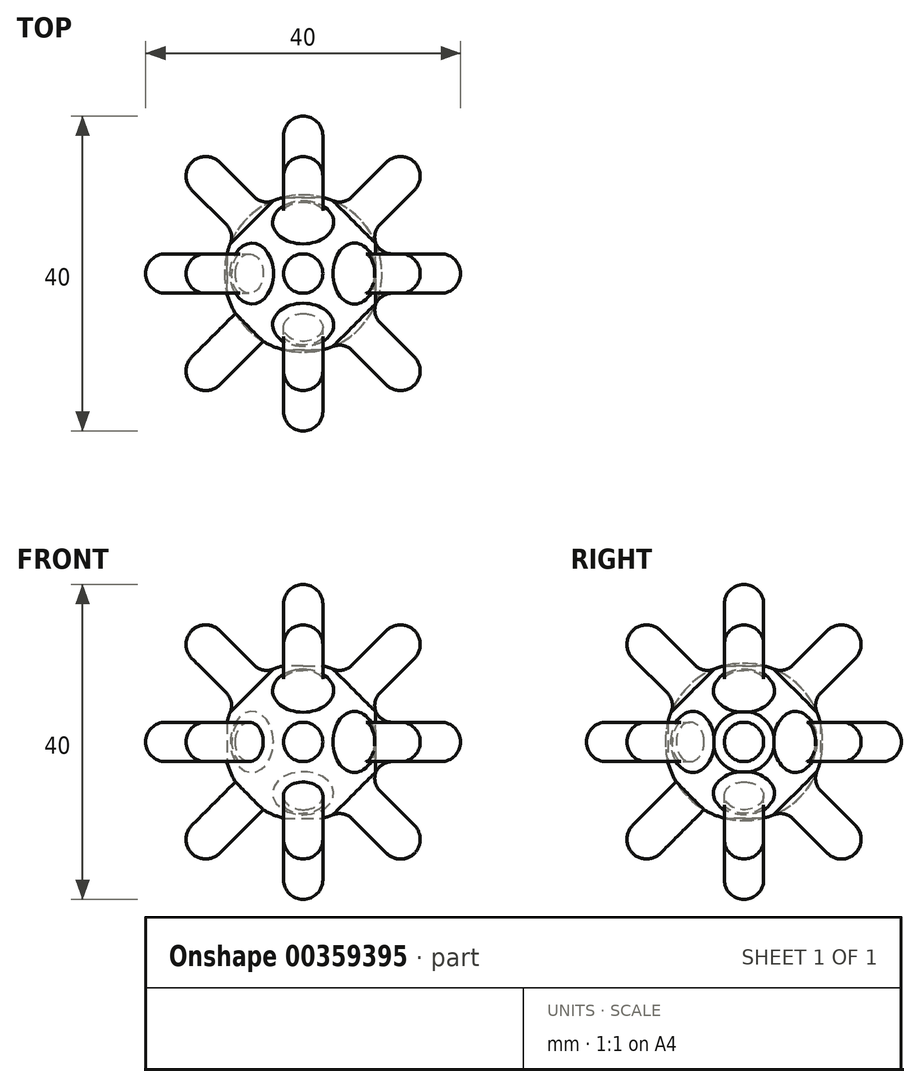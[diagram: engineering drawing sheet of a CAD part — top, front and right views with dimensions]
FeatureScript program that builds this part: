
annotation { "Feature Type Name" : "Feature", "Feature Type Description" : "" }
export const myFeature = defineFeature(function(context is Context, id is Id, definition is map)
    precondition{}
    {
        {
            var Q0;
            Q0=qCreatedBy(makeId("Front.planeOp"),FACE);
            var sketch = newSketch(context, id + "F0", { "sketchPlane" : qUnion([Q0])});
            skCircle(sketch, "E0", {"center": v(0, 0) * mm, "radius": 10 * mm});
            skSolve(sketch);
        }
        {
            var Q0;
            Q0=makeQuery(id+"F0.imprint","IMPRINT",FACE,{"disambiguationData":[TD([[makeQuery(id+"F0.imprint","IMPRINT",EDGE,{"derivedFrom":sQuery(id+"F0.wireOp",EDGE,"E0")}),1.0]])]});
            extrude(context, id + "F1", {"entities" : qUnion([Q0]), "endBound" : BoundingType.SYMMETRIC, "depth" : 20 * mm});
        }
        {
            var Q0;
            Q0=makeQuery(id+"F1.opExtrude","CAP_FACE",FACE,{"disambiguationData":[OSD([sQuery(id+"F0.wireOp",EDGE,"E0")])],"isStart":false});
            fillet(context, id + "F2", {"entities" : qUnion([Q0]), "radius" : 10 * mm, "tangentPropagation" : true, "allowEdgeOverflow" : false});
        }
        {
            var Q0;
            Q0=makeQuery(id+"F1.opExtrude","CAP_FACE",FACE,{"disambiguationData":[OSD([sQuery(id+"F0.wireOp",EDGE,"E0")])],"isStart":true});
            fillet(context, id + "F3", {"entities" : qUnion([Q0]), "radius" : 10 * mm, "tangentPropagation" : true, "allowEdgeOverflow" : false});
        }
        {
            var Q0;
            Q0=qCreatedBy(makeId("Front.planeOp"),FACE);
            var sketch = newSketch(context, id + "F4", { "sketchPlane" : qUnion([Q0])});
            skLineSegment(sketch, "E1", {"start": v(-14.14, 14.14) * mm, "end": v(-12.37, 15.9) * mm});
            skLineSegment(sketch, "E2", {"start": v(-14.14, 14.14) * mm, "end": v(-15.9, 12.37) * mm});
            skLineSegment(sketch, "E3", {"start": v(-20, 0) * mm, "end": v(-20, 2.5) * mm});
            skLineSegment(sketch, "E4", {"start": v(-20, 0) * mm, "end": v(-20, -2.5) * mm});
            skLineSegment(sketch, "E5", {"start": v(-14.14, -14.14) * mm, "end": v(-15.9, -12.37) * mm});
            skLineSegment(sketch, "E6", {"start": v(-14.14, -14.14) * mm, "end": v(-12.37, -15.9) * mm});
            skLineSegment(sketch, "E7", {"start": v(0, -20) * mm, "end": v(2.5, -20) * mm});
            skLineSegment(sketch, "E8", {"start": v(0, -20) * mm, "end": v(-2.5, -20) * mm});
            skLineSegment(sketch, "E9", {"start": v(14.14, -14.14) * mm, "end": v(12.37, -15.9) * mm});
            skLineSegment(sketch, "E10", {"start": v(14.14, -14.14) * mm, "end": v(15.9, -12.37) * mm});
            skLineSegment(sketch, "E11", {"start": v(20, 0) * mm, "end": v(20, -2.5) * mm});
            skLineSegment(sketch, "E12", {"start": v(20, 0) * mm, "end": v(20, 2.5) * mm});
            skLineSegment(sketch, "E13", {"start": v(0, 20) * mm, "end": v(2.5, 20) * mm});
            skLineSegment(sketch, "E14", {"start": v(0, 20) * mm, "end": v(-2.5, 20) * mm});
            skLineSegment(sketch, "E15", {"start": v(14.14, 14.14) * mm, "end": v(15.9, 12.37) * mm});
            skLineSegment(sketch, "E16", {"start": v(14.14, 14.14) * mm, "end": v(12.37, 15.9) * mm});
            skLineSegment(sketch, "E17", {"start": v(-15.9, 12.37) * mm, "end": v(-6.04, 2.5) * mm});
            skLineSegment(sketch, "E18", {"start": v(15.9, -12.37) * mm, "end": v(6.04, -2.5) * mm});
            skLineSegment(sketch, "E19", {"start": v(2.5, 20) * mm, "end": v(2.5, 6.04) * mm});
            skLineSegment(sketch, "E20", {"start": v(-2.5, 20) * mm, "end": v(-2.5, 6.04) * mm});
            skLineSegment(sketch, "E21", {"start": v(12.37, 15.9) * mm, "end": v(2.5, 6.04) * mm});
            skLineSegment(sketch, "E22", {"start": v(15.9, 12.37) * mm, "end": v(6.04, 2.5) * mm});
            skLineSegment(sketch, "E23", {"start": v(20, 2.5) * mm, "end": v(6.04, 2.5) * mm});
            skLineSegment(sketch, "E24", {"start": v(20, -2.5) * mm, "end": v(6.04, -2.5) * mm});
            skLineSegment(sketch, "E25.trimOffspring", {"start": v(-6.04, 2.5) * mm, "end": v(-20, 2.5) * mm});
            skLineSegment(sketch, "E26.trimOffspring", {"start": v(-2.5, 6.04) * mm, "end": v(-12.37, 15.9) * mm});
            skLineSegment(sketch, "E27.trimOffspring", {"start": v(-6.04, -2.5) * mm, "end": v(-15.9, -12.37) * mm});
            skLineSegment(sketch, "E28.trimOffspring", {"start": v(-6.04, -2.5) * mm, "end": v(-20, -2.5) * mm});
            skLineSegment(sketch, "E29.trimOffspring", {"start": v(-2.5, -6.04) * mm, "end": v(-2.5, -20) * mm});
            skLineSegment(sketch, "E30.trimOffspring", {"start": v(-2.5, -6.04) * mm, "end": v(-12.37, -15.9) * mm});
            skLineSegment(sketch, "E31.trimOffspring", {"start": v(2.5, -6.04) * mm, "end": v(12.37, -15.9) * mm});
            skLineSegment(sketch, "E32.trimOffspring", {"start": v(2.5, -6.04) * mm, "end": v(2.5, -20) * mm});
            skSolve(sketch);
        }
        {
            var Q0;
            Q0 = qSketchRegion(id + "F4", true);
            extrude(context, id + "F5", {"entities" : qUnion([Q0]), "operationType" : NewBodyOperationType.ADD, "endBound" : BoundingType.SYMMETRIC, "depth" : 5 * mm});
        }
        {
            var Q0;
            Q0=qCreatedBy(makeId("Top.planeOp"),FACE);
            var sketch = newSketch(context, id + "F6", { "sketchPlane" : qUnion([Q0])});
            skLineSegment(sketch, "E33", {"start": v(-14.14, 14.14) * mm, "end": v(-12.37, 15.9) * mm});
            skLineSegment(sketch, "E34", {"start": v(-14.14, 14.14) * mm, "end": v(-15.9, 12.37) * mm});
            skLineSegment(sketch, "E35", {"start": v(-20, 0) * mm, "end": v(-20, 2.5) * mm});
            skLineSegment(sketch, "E36", {"start": v(-20, 0) * mm, "end": v(-20, -2.5) * mm});
            skLineSegment(sketch, "E37", {"start": v(-14.14, -14.14) * mm, "end": v(-15.9, -12.37) * mm});
            skLineSegment(sketch, "E38", {"start": v(-14.14, -14.14) * mm, "end": v(-12.37, -15.9) * mm});
            skLineSegment(sketch, "E39", {"start": v(0, -20) * mm, "end": v(2.5, -20) * mm});
            skLineSegment(sketch, "E40", {"start": v(0, -20) * mm, "end": v(-2.5, -20) * mm});
            skLineSegment(sketch, "E41", {"start": v(14.14, -14.14) * mm, "end": v(12.37, -15.9) * mm});
            skLineSegment(sketch, "E42", {"start": v(14.14, -14.14) * mm, "end": v(15.9, -12.37) * mm});
            skLineSegment(sketch, "E43", {"start": v(20, 0) * mm, "end": v(20, -2.5) * mm});
            skLineSegment(sketch, "E44", {"start": v(20, 0) * mm, "end": v(20, 2.5) * mm});
            skLineSegment(sketch, "E45", {"start": v(0, 20) * mm, "end": v(2.5, 20) * mm});
            skLineSegment(sketch, "E46", {"start": v(0, 20) * mm, "end": v(-2.5, 20) * mm});
            skLineSegment(sketch, "E47", {"start": v(14.14, 14.14) * mm, "end": v(15.9, 12.37) * mm});
            skLineSegment(sketch, "E48", {"start": v(14.14, 14.14) * mm, "end": v(12.37, 15.9) * mm});
            skLineSegment(sketch, "E49", {"start": v(-15.9, 12.37) * mm, "end": v(-6.04, 2.5) * mm});
            skLineSegment(sketch, "E50", {"start": v(15.9, -12.37) * mm, "end": v(6.04, -2.5) * mm});
            skLineSegment(sketch, "E51", {"start": v(2.5, 20) * mm, "end": v(2.5, 6.04) * mm});
            skLineSegment(sketch, "E52", {"start": v(-2.5, 20) * mm, "end": v(-2.5, 6.04) * mm});
            skLineSegment(sketch, "E53", {"start": v(12.37, 15.9) * mm, "end": v(2.5, 6.04) * mm});
            skLineSegment(sketch, "E54", {"start": v(15.9, 12.37) * mm, "end": v(6.04, 2.5) * mm});
            skLineSegment(sketch, "E55", {"start": v(20, 2.5) * mm, "end": v(6.04, 2.5) * mm});
            skLineSegment(sketch, "E56", {"start": v(20, -2.5) * mm, "end": v(6.04, -2.5) * mm});
            skLineSegment(sketch, "E57.trimOffspring", {"start": v(-6.04, 2.5) * mm, "end": v(-20, 2.5) * mm});
            skLineSegment(sketch, "E58.trimOffspring", {"start": v(-2.5, 6.04) * mm, "end": v(-12.37, 15.9) * mm});
            skLineSegment(sketch, "E59.trimOffspring", {"start": v(-6.04, -2.5) * mm, "end": v(-15.9, -12.37) * mm});
            skLineSegment(sketch, "E60.trimOffspring", {"start": v(-6.04, -2.5) * mm, "end": v(-20, -2.5) * mm});
            skLineSegment(sketch, "E61.trimOffspring", {"start": v(-2.5, -6.04) * mm, "end": v(-2.5, -20) * mm});
            skLineSegment(sketch, "E62.trimOffspring", {"start": v(-2.5, -6.04) * mm, "end": v(-12.37, -15.9) * mm});
            skLineSegment(sketch, "E63.trimOffspring", {"start": v(2.5, -6.04) * mm, "end": v(12.37, -15.9) * mm});
            skLineSegment(sketch, "E64.trimOffspring", {"start": v(2.5, -6.04) * mm, "end": v(2.5, -20) * mm});
            skSolve(sketch);
        }
        {
            var Q0;
            Q0=makeQuery(id+"F6.imprint","IMPRINT",FACE,{"disambiguationData":[TD([[makeQuery(id+"F6.imprint","IMPRINT",EDGE,{"derivedFrom":sQuery(id+"F6.wireOp",EDGE,"E33")}),-1.0]])]});
            extrude(context, id + "F7", {"entities" : qUnion([Q0]), "operationType" : NewBodyOperationType.ADD, "endBound" : BoundingType.SYMMETRIC, "depth" : 5 * mm});
        }
        {
            var Q0;
            Q0=qCreatedBy(makeId("Right.planeOp"),FACE);
            var sketch = newSketch(context, id + "F8", { "sketchPlane" : qUnion([Q0])});
            skLineSegment(sketch, "E65", {"start": v(-14.14, 14.14) * mm, "end": v(-12.37, 15.9) * mm});
            skLineSegment(sketch, "E66", {"start": v(-14.14, 14.14) * mm, "end": v(-15.9, 12.37) * mm});
            skLineSegment(sketch, "E67", {"start": v(-20, 0) * mm, "end": v(-20, 2.5) * mm});
            skLineSegment(sketch, "E68", {"start": v(-20, 0) * mm, "end": v(-20, -2.5) * mm});
            skLineSegment(sketch, "E69", {"start": v(-14.14, -14.14) * mm, "end": v(-15.9, -12.37) * mm});
            skLineSegment(sketch, "E70", {"start": v(-14.14, -14.14) * mm, "end": v(-12.37, -15.9) * mm});
            skLineSegment(sketch, "E71", {"start": v(0, -20) * mm, "end": v(2.5, -20) * mm});
            skLineSegment(sketch, "E72", {"start": v(0, -20) * mm, "end": v(-2.5, -20) * mm});
            skLineSegment(sketch, "E73", {"start": v(14.14, -14.14) * mm, "end": v(12.37, -15.9) * mm});
            skLineSegment(sketch, "E74", {"start": v(14.14, -14.14) * mm, "end": v(15.9, -12.37) * mm});
            skLineSegment(sketch, "E75", {"start": v(20, 0) * mm, "end": v(20, -2.5) * mm});
            skLineSegment(sketch, "E76", {"start": v(20, 0) * mm, "end": v(20, 2.5) * mm});
            skLineSegment(sketch, "E77", {"start": v(0, 20) * mm, "end": v(2.5, 20) * mm});
            skLineSegment(sketch, "E78", {"start": v(0, 20) * mm, "end": v(-2.5, 20) * mm});
            skLineSegment(sketch, "E79", {"start": v(14.14, 14.14) * mm, "end": v(15.9, 12.37) * mm});
            skLineSegment(sketch, "E80", {"start": v(14.14, 14.14) * mm, "end": v(12.37, 15.9) * mm});
            skLineSegment(sketch, "E81", {"start": v(-15.9, 12.37) * mm, "end": v(-6.04, 2.5) * mm});
            skLineSegment(sketch, "E82", {"start": v(15.9, -12.37) * mm, "end": v(6.04, -2.5) * mm});
            skLineSegment(sketch, "E83", {"start": v(2.5, 20) * mm, "end": v(2.5, 6.04) * mm});
            skLineSegment(sketch, "E84", {"start": v(-2.5, 20) * mm, "end": v(-2.5, 6.04) * mm});
            skLineSegment(sketch, "E85", {"start": v(12.37, 15.9) * mm, "end": v(2.5, 6.04) * mm});
            skLineSegment(sketch, "E86", {"start": v(15.9, 12.37) * mm, "end": v(6.04, 2.5) * mm});
            skLineSegment(sketch, "E87", {"start": v(20, 2.5) * mm, "end": v(6.04, 2.5) * mm});
            skLineSegment(sketch, "E88", {"start": v(20, -2.5) * mm, "end": v(6.04, -2.5) * mm});
            skLineSegment(sketch, "E89.trimOffspring", {"start": v(-6.04, 2.5) * mm, "end": v(-20, 2.5) * mm});
            skLineSegment(sketch, "E90.trimOffspring", {"start": v(-2.5, 6.04) * mm, "end": v(-12.37, 15.9) * mm});
            skLineSegment(sketch, "E91.trimOffspring", {"start": v(-6.04, -2.5) * mm, "end": v(-15.9, -12.37) * mm});
            skLineSegment(sketch, "E92.trimOffspring", {"start": v(-6.04, -2.5) * mm, "end": v(-20, -2.5) * mm});
            skLineSegment(sketch, "E93.trimOffspring", {"start": v(-2.5, -6.04) * mm, "end": v(-2.5, -20) * mm});
            skLineSegment(sketch, "E94.trimOffspring", {"start": v(-2.5, -6.04) * mm, "end": v(-12.37, -15.9) * mm});
            skLineSegment(sketch, "E95.trimOffspring", {"start": v(2.5, -6.04) * mm, "end": v(12.37, -15.9) * mm});
            skLineSegment(sketch, "E96.trimOffspring", {"start": v(2.5, -6.04) * mm, "end": v(2.5, -20) * mm});
            skSolve(sketch);
        }
        {
            var Q0;
            Q0 = qSketchRegion(id + "F8", true);
            extrude(context, id + "F9", {"entities" : qUnion([Q0]), "operationType" : NewBodyOperationType.ADD, "endBound" : BoundingType.SYMMETRIC, "depth" : 5 * mm});
        }
        {
            var Q0;
            Q0=makeQuery(id+"F5.opExtrude","CAP_EDGE",EDGE,{"disambiguationData":[OSD([sQuery(id+"F4.wireOp",EDGE,"E23")])],"isStart":false});
            var Q1;
            Q1=makeQuery(id+"F5.opExtrude","CAP_EDGE",EDGE,{"disambiguationData":[OSD([sQuery(id+"F4.wireOp",EDGE,"E24")])],"isStart":false});
            var Q2;
            Q2=makeQuery(id+"F5.opExtrude","CAP_EDGE",EDGE,{"disambiguationData":[OSD([sQuery(id+"F4.wireOp",EDGE,"E23")])],"isStart":true});
            var Q3;
            Q3=makeQuery(id+"F5.opExtrude","CAP_EDGE",EDGE,{"disambiguationData":[OSD([sQuery(id+"F4.wireOp",EDGE,"E24")])],"isStart":true});
            var Q4;
            Q4=makeQuery(id+"F5.opExtrude","SWEPT_FACE",FACE,{"disambiguationData":[OSD([sQuery(id+"F4.wireOp",EDGE,"E11"),sQuery(id+"F4.wireOp",EDGE,"E12")])]});
            fillet(context, id + "F10", {"entities" : qUnion([Q0, Q1, Q2, Q3, Q4]), "radius" : 2.5 * mm, "tangentPropagation" : true, "allowEdgeOverflow" : false});
        }
        {
            var Q0;
            Q0=makeQuery(id+"F5.opExtrude","SWEPT_FACE",FACE,{"disambiguationData":[OSD([sQuery(id+"F4.wireOp",EDGE,"E9"),sQuery(id+"F4.wireOp",EDGE,"E10")])]});
            var Q1;
            Q1=makeQuery(id+"F5.opExtrude","CAP_EDGE",EDGE,{"disambiguationData":[OSD([sQuery(id+"F4.wireOp",EDGE,"E31.trimOffspring")])],"isStart":false});
            var Q2;
            Q2=makeQuery(id+"F5.opExtrude","CAP_EDGE",EDGE,{"disambiguationData":[OSD([sQuery(id+"F4.wireOp",EDGE,"E31.trimOffspring")])],"isStart":true});
            var Q3;
            Q3=makeQuery(id+"F5.opExtrude","CAP_EDGE",EDGE,{"disambiguationData":[OSD([sQuery(id+"F4.wireOp",EDGE,"E18")])],"isStart":false});
            var Q4;
            Q4=makeQuery(id+"F5.opExtrude","CAP_EDGE",EDGE,{"disambiguationData":[OSD([sQuery(id+"F4.wireOp",EDGE,"E18")])],"isStart":true});
            fillet(context, id + "F11", {"entities" : qUnion([Q0, Q1, Q2, Q3, Q4]), "radius" : 2.5 * mm, "tangentPropagation" : true, "allowEdgeOverflow" : false});
        }
        {
            var Q0;
            Q0=makeQuery(id+"F5.opExtrude","CAP_EDGE",EDGE,{"disambiguationData":[OSD([sQuery(id+"F4.wireOp",EDGE,"E22")])],"isStart":false});
            var Q1;
            Q1=makeQuery(id+"F5.opExtrude","CAP_EDGE",EDGE,{"disambiguationData":[OSD([sQuery(id+"F4.wireOp",EDGE,"E22")])],"isStart":true});
            var Q2;
            Q2=makeQuery(id+"F5.opExtrude","CAP_EDGE",EDGE,{"disambiguationData":[OSD([sQuery(id+"F4.wireOp",EDGE,"E21")])],"isStart":false});
            var Q3;
            Q3=makeQuery(id+"F5.opExtrude","CAP_EDGE",EDGE,{"disambiguationData":[OSD([sQuery(id+"F4.wireOp",EDGE,"E21")])],"isStart":true});
            var Q4;
            Q4=makeQuery(id+"F5.opExtrude","SWEPT_FACE",FACE,{"disambiguationData":[OSD([sQuery(id+"F4.wireOp",EDGE,"E15"),sQuery(id+"F4.wireOp",EDGE,"E16")])]});
            fillet(context, id + "F12", {"entities" : qUnion([Q0, Q1, Q2, Q3, Q4]), "radius" : 2.5 * mm, "tangentPropagation" : true, "allowEdgeOverflow" : false});
        }
        {
            var Q0;
            Q0=makeQuery(id+"F5.opExtrude","CAP_EDGE",EDGE,{"disambiguationData":[OSD([sQuery(id+"F4.wireOp",EDGE,"E19")])],"isStart":false});
            var Q1;
            Q1=makeQuery(id+"F5.opExtrude","CAP_EDGE",EDGE,{"disambiguationData":[OSD([sQuery(id+"F4.wireOp",EDGE,"E20")])],"isStart":false});
            var Q2;
            Q2=makeQuery(id+"F5.opExtrude","CAP_EDGE",EDGE,{"disambiguationData":[OSD([sQuery(id+"F4.wireOp",EDGE,"E19")])],"isStart":true});
            var Q3;
            Q3=makeQuery(id+"F5.opExtrude","CAP_EDGE",EDGE,{"disambiguationData":[OSD([sQuery(id+"F4.wireOp",EDGE,"E20")])],"isStart":true});
            var Q4;
            Q4=makeQuery(id+"F5.opExtrude","SWEPT_FACE",FACE,{"disambiguationData":[OSD([sQuery(id+"F4.wireOp",EDGE,"E13"),sQuery(id+"F4.wireOp",EDGE,"E14")])]});
            fillet(context, id + "F13", {"entities" : qUnion([Q0, Q1, Q2, Q3, Q4]), "radius" : 2.5 * mm, "tangentPropagation" : true, "allowEdgeOverflow" : false});
        }
        {
            var Q0;
            Q0=makeQuery(id+"F5.opExtrude","CAP_EDGE",EDGE,{"disambiguationData":[OSD([sQuery(id+"F4.wireOp",EDGE,"E32.trimOffspring")])],"isStart":false});
            var Q1;
            Q1=makeQuery(id+"F5.opExtrude","CAP_EDGE",EDGE,{"disambiguationData":[OSD([sQuery(id+"F4.wireOp",EDGE,"E32.trimOffspring")])],"isStart":true});
            var Q2;
            Q2=makeQuery(id+"F5.opExtrude","CAP_EDGE",EDGE,{"disambiguationData":[OSD([sQuery(id+"F4.wireOp",EDGE,"E29.trimOffspring")])],"isStart":false});
            var Q3;
            Q3=makeQuery(id+"F5.opExtrude","CAP_EDGE",EDGE,{"disambiguationData":[OSD([sQuery(id+"F4.wireOp",EDGE,"E29.trimOffspring")])],"isStart":true});
            var Q4;
            Q4=makeQuery(id+"F5.opExtrude","SWEPT_FACE",FACE,{"disambiguationData":[OSD([sQuery(id+"F4.wireOp",EDGE,"E7"),sQuery(id+"F4.wireOp",EDGE,"E8")])]});
            fillet(context, id + "F14", {"entities" : qUnion([Q0, Q1, Q2, Q3, Q4]), "radius" : 2.5 * mm, "tangentPropagation" : true, "allowEdgeOverflow" : false});
        }
        {
            var Q0;
            Q0=makeQuery(id+"F5.opExtrude","CAP_EDGE",EDGE,{"disambiguationData":[OSD([sQuery(id+"F4.wireOp",EDGE,"E27.trimOffspring")])],"isStart":true});
            var Q1;
            Q1=makeQuery(id+"F5.opExtrude","CAP_EDGE",EDGE,{"disambiguationData":[OSD([sQuery(id+"F4.wireOp",EDGE,"E27.trimOffspring")])],"isStart":false});
            var Q2;
            Q2=makeQuery(id+"F5.opExtrude","CAP_EDGE",EDGE,{"disambiguationData":[OSD([sQuery(id+"F4.wireOp",EDGE,"E30.trimOffspring")])],"isStart":true});
            var Q3;
            Q3=makeQuery(id+"F5.opExtrude","CAP_EDGE",EDGE,{"disambiguationData":[OSD([sQuery(id+"F4.wireOp",EDGE,"E30.trimOffspring")])],"isStart":false});
            var Q4;
            Q4=makeQuery(id+"F5.opExtrude","SWEPT_FACE",FACE,{"disambiguationData":[OSD([sQuery(id+"F4.wireOp",EDGE,"E5"),sQuery(id+"F4.wireOp",EDGE,"E6")])]});
            fillet(context, id + "F15", {"entities" : qUnion([Q0, Q1, Q2, Q3, Q4]), "radius" : 2.5 * mm, "tangentPropagation" : true, "allowEdgeOverflow" : false});
        }
        {
            var Q0;
            Q0=makeQuery(id+"F5.opExtrude","CAP_EDGE",EDGE,{"disambiguationData":[OSD([sQuery(id+"F4.wireOp",EDGE,"E28.trimOffspring")])],"isStart":false});
            var Q1;
            Q1=makeQuery(id+"F5.opExtrude","CAP_EDGE",EDGE,{"disambiguationData":[OSD([sQuery(id+"F4.wireOp",EDGE,"E28.trimOffspring")])],"isStart":true});
            var Q2;
            Q2=makeQuery(id+"F5.opExtrude","CAP_EDGE",EDGE,{"disambiguationData":[OSD([sQuery(id+"F4.wireOp",EDGE,"E25.trimOffspring")])],"isStart":false});
            var Q3;
            Q3=makeQuery(id+"F5.opExtrude","CAP_EDGE",EDGE,{"disambiguationData":[OSD([sQuery(id+"F4.wireOp",EDGE,"E25.trimOffspring")])],"isStart":true});
            var Q4;
            Q4=makeQuery(id+"F5.opExtrude","SWEPT_FACE",FACE,{"disambiguationData":[OSD([sQuery(id+"F4.wireOp",EDGE,"E3"),sQuery(id+"F4.wireOp",EDGE,"E4")])]});
            fillet(context, id + "F16", {"entities" : qUnion([Q0, Q1, Q2, Q3, Q4]), "radius" : 2.5 * mm, "tangentPropagation" : true, "allowEdgeOverflow" : false});
        }
        {
            var Q0;
            Q0=makeQuery(id+"F5.opExtrude","CAP_EDGE",EDGE,{"disambiguationData":[OSD([sQuery(id+"F4.wireOp",EDGE,"E26.trimOffspring")])],"isStart":false});
            var Q1;
            Q1=makeQuery(id+"F5.opExtrude","CAP_EDGE",EDGE,{"disambiguationData":[OSD([sQuery(id+"F4.wireOp",EDGE,"E26.trimOffspring")])],"isStart":true});
            var Q2;
            Q2=makeQuery(id+"F5.opExtrude","CAP_EDGE",EDGE,{"disambiguationData":[OSD([sQuery(id+"F4.wireOp",EDGE,"E17")])],"isStart":false});
            var Q3;
            Q3=makeQuery(id+"F5.opExtrude","SWEPT_FACE",FACE,{"disambiguationData":[OSD([sQuery(id+"F4.wireOp",EDGE,"E1"),sQuery(id+"F4.wireOp",EDGE,"E2")])]});
            var Q4;
            Q4=makeQuery(id+"F5.opExtrude","CAP_EDGE",EDGE,{"disambiguationData":[OSD([sQuery(id+"F4.wireOp",EDGE,"E17")])],"isStart":true});
            fillet(context, id + "F17", {"entities" : qUnion([Q0, Q1, Q2, Q3, Q4]), "radius" : 2.5 * mm, "tangentPropagation" : true, "allowEdgeOverflow" : false});
        }
        {
            var Q0;
            Q0=makeQuery(id+"F9.opExtrude","CAP_EDGE",EDGE,{"disambiguationData":[OSD([sQuery(id+"F8.wireOp",EDGE,"E95.trimOffspring")])],"isStart":false});
            var Q1;
            Q1=makeQuery(id+"F9.opExtrude","CAP_EDGE",EDGE,{"disambiguationData":[OSD([sQuery(id+"F8.wireOp",EDGE,"E82")])],"isStart":false});
            var Q2;
            Q2=makeQuery(id+"F9.opExtrude","SWEPT_FACE",FACE,{"disambiguationData":[OSD([sQuery(id+"F8.wireOp",EDGE,"E73"),sQuery(id+"F8.wireOp",EDGE,"E74")])]});
            var Q3;
            Q3=makeQuery(id+"F9.opExtrude","CAP_EDGE",EDGE,{"disambiguationData":[OSD([sQuery(id+"F8.wireOp",EDGE,"E82")])],"isStart":true});
            var Q4;
            Q4=makeQuery(id+"F9.opExtrude","CAP_EDGE",EDGE,{"disambiguationData":[OSD([sQuery(id+"F8.wireOp",EDGE,"E95.trimOffspring")])],"isStart":true});
            fillet(context, id + "F18", {"entities" : qUnion([Q0, Q1, Q2, Q3, Q4]), "radius" : 2.5 * mm, "tangentPropagation" : true, "allowEdgeOverflow" : false});
        }
        {
            var Q0;
            Q0=makeQuery(id+"F7.opExtrude","CAP_EDGE",EDGE,{"disambiguationData":[OSD([sQuery(id+"F6.wireOp",EDGE,"E52")])],"isStart":false});
            var Q1;
            Q1=makeQuery(id+"F7.opExtrude","CAP_EDGE",EDGE,{"disambiguationData":[OSD([sQuery(id+"F6.wireOp",EDGE,"E52")])],"isStart":true});
            var Q2;
            Q2=makeQuery(id+"F7.opExtrude","CAP_EDGE",EDGE,{"disambiguationData":[OSD([sQuery(id+"F6.wireOp",EDGE,"E51")])],"isStart":false});
            var Q3;
            Q3=makeQuery(id+"F7.opExtrude","CAP_EDGE",EDGE,{"disambiguationData":[OSD([sQuery(id+"F6.wireOp",EDGE,"E51")])],"isStart":true});
            var Q4;
            Q4=makeQuery(id+"F7.opExtrude","SWEPT_FACE",FACE,{"disambiguationData":[OSD([sQuery(id+"F6.wireOp",EDGE,"E45"),sQuery(id+"F6.wireOp",EDGE,"E46")])]});
            fillet(context, id + "F19", {"entities" : qUnion([Q0, Q1, Q2, Q3, Q4]), "radius" : 2.5 * mm, "tangentPropagation" : true, "allowEdgeOverflow" : false});
        }
        {
            var Q0;
            Q0=makeQuery(id+"F9.opExtrude","CAP_EDGE",EDGE,{"disambiguationData":[OSD([sQuery(id+"F8.wireOp",EDGE,"E85")])],"isStart":true});
            var Q1;
            Q1=makeQuery(id+"F9.opExtrude","CAP_EDGE",EDGE,{"disambiguationData":[OSD([sQuery(id+"F8.wireOp",EDGE,"E85")])],"isStart":false});
            var Q2;
            Q2=makeQuery(id+"F9.opExtrude","CAP_EDGE",EDGE,{"disambiguationData":[OSD([sQuery(id+"F8.wireOp",EDGE,"E86")])],"isStart":true});
            var Q3;
            Q3=makeQuery(id+"F9.opExtrude","CAP_EDGE",EDGE,{"disambiguationData":[OSD([sQuery(id+"F8.wireOp",EDGE,"E86")])],"isStart":false});
            var Q4;
            Q4=makeQuery(id+"F9.opExtrude","SWEPT_FACE",FACE,{"disambiguationData":[OSD([sQuery(id+"F8.wireOp",EDGE,"E79"),sQuery(id+"F8.wireOp",EDGE,"E80")])]});
            fillet(context, id + "F20", {"entities" : qUnion([Q0, Q1, Q2, Q3, Q4]), "radius" : 2.5 * mm, "tangentPropagation" : true, "allowEdgeOverflow" : false});
        }
        {
            var Q0;
            Q0=makeQuery(id+"F9.opExtrude","CAP_EDGE",EDGE,{"disambiguationData":[OSD([sQuery(id+"F8.wireOp",EDGE,"E81")])],"isStart":true});
            var Q1;
            Q1=makeQuery(id+"F9.opExtrude","CAP_EDGE",EDGE,{"disambiguationData":[OSD([sQuery(id+"F8.wireOp",EDGE,"E81")])],"isStart":false});
            var Q2;
            Q2=makeQuery(id+"F9.opExtrude","CAP_EDGE",EDGE,{"disambiguationData":[OSD([sQuery(id+"F8.wireOp",EDGE,"E90.trimOffspring")])],"isStart":false});
            var Q3;
            Q3=makeQuery(id+"F9.opExtrude","CAP_EDGE",EDGE,{"disambiguationData":[OSD([sQuery(id+"F8.wireOp",EDGE,"E90.trimOffspring")])],"isStart":true});
            var Q4;
            Q4=makeQuery(id+"F9.opExtrude","SWEPT_FACE",FACE,{"disambiguationData":[OSD([sQuery(id+"F8.wireOp",EDGE,"E65"),sQuery(id+"F8.wireOp",EDGE,"E66")])]});
            fillet(context, id + "F21", {"entities" : qUnion([Q0, Q1, Q2, Q3, Q4]), "radius" : 2.5 * mm, "tangentPropagation" : true, "allowEdgeOverflow" : false});
        }
        {
            var Q0;
            Q0=makeQuery(id+"F7.opExtrude","CAP_EDGE",EDGE,{"disambiguationData":[OSD([sQuery(id+"F6.wireOp",EDGE,"E64.trimOffspring")])],"isStart":false});
            var Q1;
            Q1=makeQuery(id+"F7.opExtrude","CAP_EDGE",EDGE,{"disambiguationData":[OSD([sQuery(id+"F6.wireOp",EDGE,"E61.trimOffspring")])],"isStart":false});
            var Q2;
            Q2=makeQuery(id+"F7.opExtrude","CAP_EDGE",EDGE,{"disambiguationData":[OSD([sQuery(id+"F6.wireOp",EDGE,"E61.trimOffspring")])],"isStart":true});
            var Q3;
            Q3=makeQuery(id+"F7.opExtrude","CAP_EDGE",EDGE,{"disambiguationData":[OSD([sQuery(id+"F6.wireOp",EDGE,"E64.trimOffspring")])],"isStart":true});
            var Q4;
            Q4=makeQuery(id+"F7.opExtrude","SWEPT_FACE",FACE,{"disambiguationData":[OSD([sQuery(id+"F6.wireOp",EDGE,"E39"),sQuery(id+"F6.wireOp",EDGE,"E40")])]});
            fillet(context, id + "F22", {"entities" : qUnion([Q0, Q1, Q2, Q3, Q4]), "radius" : 2.5 * mm, "tangentPropagation" : true, "allowEdgeOverflow" : false});
        }
        {
            var Q0;
            Q0=makeQuery(id+"F9.opExtrude","CAP_EDGE",EDGE,{"disambiguationData":[OSD([sQuery(id+"F8.wireOp",EDGE,"E91.trimOffspring")])],"isStart":true});
            var Q1;
            Q1=makeQuery(id+"F9.opExtrude","CAP_EDGE",EDGE,{"disambiguationData":[OSD([sQuery(id+"F8.wireOp",EDGE,"E91.trimOffspring")])],"isStart":false});
            var Q2;
            Q2=makeQuery(id+"F9.opExtrude","CAP_EDGE",EDGE,{"disambiguationData":[OSD([sQuery(id+"F8.wireOp",EDGE,"E94.trimOffspring")])],"isStart":true});
            var Q3;
            Q3=makeQuery(id+"F9.opExtrude","CAP_EDGE",EDGE,{"disambiguationData":[OSD([sQuery(id+"F8.wireOp",EDGE,"E94.trimOffspring")])],"isStart":false});
            var Q4;
            Q4=makeQuery(id+"F9.opExtrude","SWEPT_FACE",FACE,{"disambiguationData":[OSD([sQuery(id+"F8.wireOp",EDGE,"E69"),sQuery(id+"F8.wireOp",EDGE,"E70")])]});
            fillet(context, id + "F23", {"entities" : qUnion([Q0, Q1, Q2, Q3, Q4]), "radius" : 2.5 * mm, "tangentPropagation" : true, "allowEdgeOverflow" : false});
        }
        {
            var Q0;
            Q0=makeQuery(id+"F7.opExtrude","CAP_EDGE",EDGE,{"disambiguationData":[OSD([sQuery(id+"F6.wireOp",EDGE,"E62.trimOffspring")])],"isStart":true});
            var Q1;
            Q1=makeQuery(id+"F7.opExtrude","CAP_EDGE",EDGE,{"disambiguationData":[OSD([sQuery(id+"F6.wireOp",EDGE,"E62.trimOffspring")])],"isStart":false});
            var Q2;
            Q2=makeQuery(id+"F7.opExtrude","CAP_EDGE",EDGE,{"disambiguationData":[OSD([sQuery(id+"F6.wireOp",EDGE,"E59.trimOffspring")])],"isStart":true});
            var Q3;
            Q3=makeQuery(id+"F7.opExtrude","CAP_EDGE",EDGE,{"disambiguationData":[OSD([sQuery(id+"F6.wireOp",EDGE,"E59.trimOffspring")])],"isStart":false});
            var Q4;
            Q4=makeQuery(id+"F7.opExtrude","SWEPT_FACE",FACE,{"disambiguationData":[OSD([sQuery(id+"F6.wireOp",EDGE,"E37"),sQuery(id+"F6.wireOp",EDGE,"E38")])]});
            fillet(context, id + "F24", {"entities" : qUnion([Q0, Q1, Q2, Q3, Q4]), "radius" : 2.5 * mm, "tangentPropagation" : true, "allowEdgeOverflow" : false});
        }
        {
            var Q0;
            Q0=makeQuery(id+"F7.opExtrude","CAP_EDGE",EDGE,{"disambiguationData":[OSD([sQuery(id+"F6.wireOp",EDGE,"E49")])],"isStart":true});
            var Q1;
            Q1=makeQuery(id+"F7.opExtrude","CAP_EDGE",EDGE,{"disambiguationData":[OSD([sQuery(id+"F6.wireOp",EDGE,"E49")])],"isStart":false});
            var Q2;
            Q2=makeQuery(id+"F7.opExtrude","CAP_EDGE",EDGE,{"disambiguationData":[OSD([sQuery(id+"F6.wireOp",EDGE,"E58.trimOffspring")])],"isStart":true});
            var Q3;
            Q3=makeQuery(id+"F7.opExtrude","CAP_EDGE",EDGE,{"disambiguationData":[OSD([sQuery(id+"F6.wireOp",EDGE,"E58.trimOffspring")])],"isStart":false});
            var Q4;
            Q4=makeQuery(id+"F7.opExtrude","SWEPT_FACE",FACE,{"disambiguationData":[OSD([sQuery(id+"F6.wireOp",EDGE,"E33"),sQuery(id+"F6.wireOp",EDGE,"E34")])]});
            fillet(context, id + "F25", {"entities" : qUnion([Q0, Q1, Q2, Q3, Q4]), "radius" : 2.5 * mm, "tangentPropagation" : true, "allowEdgeOverflow" : false});
        }
        {
            var Q0;
            Q0=makeQuery(id+"F7.opExtrude","CAP_EDGE",EDGE,{"disambiguationData":[OSD([sQuery(id+"F6.wireOp",EDGE,"E53")])],"isStart":true});
            var Q1;
            Q1=makeQuery(id+"F7.opExtrude","CAP_EDGE",EDGE,{"disambiguationData":[OSD([sQuery(id+"F6.wireOp",EDGE,"E53")])],"isStart":false});
            var Q2;
            Q2=makeQuery(id+"F7.opExtrude","CAP_EDGE",EDGE,{"disambiguationData":[OSD([sQuery(id+"F6.wireOp",EDGE,"E54")])],"isStart":false});
            var Q3;
            Q3=makeQuery(id+"F7.opExtrude","CAP_EDGE",EDGE,{"disambiguationData":[OSD([sQuery(id+"F6.wireOp",EDGE,"E54")])],"isStart":true});
            var Q4;
            Q4=makeQuery(id+"F7.opExtrude","SWEPT_FACE",FACE,{"disambiguationData":[OSD([sQuery(id+"F6.wireOp",EDGE,"E47"),sQuery(id+"F6.wireOp",EDGE,"E48")])]});
            fillet(context, id + "F26", {"entities" : qUnion([Q0, Q1, Q2, Q3, Q4]), "radius" : 2.5 * mm, "tangentPropagation" : true, "allowEdgeOverflow" : false});
        }
        {
            var Q0;
            Q0=makeQuery(id+"F7.opExtrude","CAP_EDGE",EDGE,{"disambiguationData":[OSD([sQuery(id+"F6.wireOp",EDGE,"E50")])],"isStart":true});
            var Q1;
            Q1=makeQuery(id+"F7.opExtrude","CAP_EDGE",EDGE,{"disambiguationData":[OSD([sQuery(id+"F6.wireOp",EDGE,"E50")])],"isStart":false});
            var Q2;
            Q2=makeQuery(id+"F7.opExtrude","CAP_EDGE",EDGE,{"disambiguationData":[OSD([sQuery(id+"F6.wireOp",EDGE,"E63.trimOffspring")])],"isStart":true});
            var Q3;
            Q3=makeQuery(id+"F7.opExtrude","CAP_EDGE",EDGE,{"disambiguationData":[OSD([sQuery(id+"F6.wireOp",EDGE,"E63.trimOffspring")])],"isStart":false});
            var Q4;
            Q4=makeQuery(id+"F7.opExtrude","SWEPT_FACE",FACE,{"disambiguationData":[OSD([sQuery(id+"F6.wireOp",EDGE,"E41"),sQuery(id+"F6.wireOp",EDGE,"E42")])]});
            fillet(context, id + "F27", {"entities" : qUnion([Q0, Q1, Q2, Q3, Q4]), "radius" : 2.5 * mm, "tangentPropagation" : true, "allowEdgeOverflow" : false});
        }
        {
            var Q0;
            Q0=makeQuery(id+"F20.opFillet","BLEND_EDGE",EDGE,{"blendedFrom":[makeQuery(id+"F9.opExtrude","CAP_EDGE",EDGE,{"disambiguationData":[OSD([sQuery(id+"F8.wireOp",EDGE,"E85")])],"isStart":true}),makeQuery(id+"F2.opFillet","BLEND_FACE",FACE,{"disambiguationData":[OSD([sQuery(id+"F0.wireOp",EDGE,"E0")])]})],"blendedInto":[makeQuery(id+"F2.opFillet","BLEND_FACE",FACE,{"disambiguationData":[OSD([sQuery(id+"F0.wireOp",EDGE,"E0")])]})]});
            var Q1;
            Q1=makeQuery(id+"F19.opFillet","BLEND_EDGE",EDGE,{"blendedFrom":[makeQuery(id+"F7.opExtrude","CAP_EDGE",EDGE,{"disambiguationData":[OSD([sQuery(id+"F6.wireOp",EDGE,"E52")])],"isStart":true}),makeQuery(id+"F2.opFillet","BLEND_FACE",FACE,{"disambiguationData":[OSD([sQuery(id+"F0.wireOp",EDGE,"E0")])]})],"blendedInto":[makeQuery(id+"F2.opFillet","BLEND_FACE",FACE,{"disambiguationData":[OSD([sQuery(id+"F0.wireOp",EDGE,"E0")])]})]});
            var Q2;
            Q2=makeQuery(id+"F13.opFillet","BLEND_EDGE",EDGE,{"blendedFrom":[makeQuery(id+"F5.opExtrude","CAP_EDGE",EDGE,{"disambiguationData":[OSD([sQuery(id+"F4.wireOp",EDGE,"E20")])],"isStart":true}),makeQuery(id+"F2.opFillet","BLEND_FACE",FACE,{"disambiguationData":[OSD([sQuery(id+"F0.wireOp",EDGE,"E0")])]})],"blendedInto":[makeQuery(id+"F2.opFillet","BLEND_FACE",FACE,{"disambiguationData":[OSD([sQuery(id+"F0.wireOp",EDGE,"E0")])]})]});
            var Q3;
            Q3=makeQuery(id+"F12.opFillet","BLEND_EDGE",EDGE,{"blendedFrom":[makeQuery(id+"F5.opExtrude","CAP_EDGE",EDGE,{"disambiguationData":[OSD([sQuery(id+"F4.wireOp",EDGE,"E21")])],"isStart":true}),makeQuery(id+"F2.opFillet","BLEND_FACE",FACE,{"disambiguationData":[OSD([sQuery(id+"F0.wireOp",EDGE,"E0")])]})],"blendedInto":[makeQuery(id+"F2.opFillet","BLEND_FACE",FACE,{"disambiguationData":[OSD([sQuery(id+"F0.wireOp",EDGE,"E0")])]})]});
            var Q4;
            Q4=makeQuery(id+"F26.opFillet","BLEND_EDGE",EDGE,{"blendedFrom":[makeQuery(id+"F7.opExtrude","CAP_EDGE",EDGE,{"disambiguationData":[OSD([sQuery(id+"F6.wireOp",EDGE,"E53")])],"isStart":true}),makeQuery(id+"F2.opFillet","BLEND_FACE",FACE,{"disambiguationData":[OSD([sQuery(id+"F0.wireOp",EDGE,"E0")])]})],"blendedInto":[makeQuery(id+"F2.opFillet","BLEND_FACE",FACE,{"disambiguationData":[OSD([sQuery(id+"F0.wireOp",EDGE,"E0")])]})]});
            var Q5;
            Q5=makeQuery(id+"F10.opFillet","BLEND_EDGE",EDGE,{"blendedFrom":[makeQuery(id+"F5.opExtrude","CAP_EDGE",EDGE,{"disambiguationData":[OSD([sQuery(id+"F4.wireOp",EDGE,"E23")])],"isStart":true}),makeQuery(id+"F2.opFillet","BLEND_FACE",FACE,{"disambiguationData":[OSD([sQuery(id+"F0.wireOp",EDGE,"E0")])]})],"blendedInto":[makeQuery(id+"F2.opFillet","BLEND_FACE",FACE,{"disambiguationData":[OSD([sQuery(id+"F0.wireOp",EDGE,"E0")])]})]});
            var Q6;
            Q6=makeQuery(id+"F25.opFillet","BLEND_EDGE",EDGE,{"blendedFrom":[makeQuery(id+"F7.opExtrude","CAP_EDGE",EDGE,{"disambiguationData":[OSD([sQuery(id+"F6.wireOp",EDGE,"E49")])],"isStart":true}),makeQuery(id+"F2.opFillet","BLEND_FACE",FACE,{"disambiguationData":[OSD([sQuery(id+"F0.wireOp",EDGE,"E0")])]})],"blendedInto":[makeQuery(id+"F2.opFillet","BLEND_FACE",FACE,{"disambiguationData":[OSD([sQuery(id+"F0.wireOp",EDGE,"E0")])]})]});
            var Q7;
            Q7=makeQuery(id+"F16.opFillet","BLEND_EDGE",EDGE,{"blendedFrom":[makeQuery(id+"F5.opExtrude","CAP_EDGE",EDGE,{"disambiguationData":[OSD([sQuery(id+"F4.wireOp",EDGE,"E28.trimOffspring")])],"isStart":true}),makeQuery(id+"F2.opFillet","BLEND_FACE",FACE,{"disambiguationData":[OSD([sQuery(id+"F0.wireOp",EDGE,"E0")])]})],"blendedInto":[makeQuery(id+"F2.opFillet","BLEND_FACE",FACE,{"disambiguationData":[OSD([sQuery(id+"F0.wireOp",EDGE,"E0")])]})]});
            var Q8;
            Q8=makeQuery(id+"F24.opFillet","BLEND_EDGE",EDGE,{"blendedFrom":[makeQuery(id+"F7.opExtrude","CAP_EDGE",EDGE,{"disambiguationData":[OSD([sQuery(id+"F6.wireOp",EDGE,"E62.trimOffspring")])],"isStart":true}),makeQuery(id+"F2.opFillet","BLEND_FACE",FACE,{"disambiguationData":[OSD([sQuery(id+"F0.wireOp",EDGE,"E0")])]})],"blendedInto":[makeQuery(id+"F2.opFillet","BLEND_FACE",FACE,{"disambiguationData":[OSD([sQuery(id+"F0.wireOp",EDGE,"E0")])]})]});
            var Q9;
            Q9=makeQuery(id+"F22.opFillet","BLEND_EDGE",EDGE,{"blendedFrom":[makeQuery(id+"F7.opExtrude","CAP_EDGE",EDGE,{"disambiguationData":[OSD([sQuery(id+"F6.wireOp",EDGE,"E64.trimOffspring")])],"isStart":true}),makeQuery(id+"F2.opFillet","BLEND_FACE",FACE,{"disambiguationData":[OSD([sQuery(id+"F0.wireOp",EDGE,"E0")])]})],"blendedInto":[makeQuery(id+"F2.opFillet","BLEND_FACE",FACE,{"disambiguationData":[OSD([sQuery(id+"F0.wireOp",EDGE,"E0")])]})]});
            var Q10;
            Q10=makeQuery(id+"F27.opFillet","BLEND_EDGE",EDGE,{"blendedFrom":[makeQuery(id+"F7.opExtrude","CAP_EDGE",EDGE,{"disambiguationData":[OSD([sQuery(id+"F6.wireOp",EDGE,"E50")])],"isStart":true}),makeQuery(id+"F2.opFillet","BLEND_FACE",FACE,{"disambiguationData":[OSD([sQuery(id+"F0.wireOp",EDGE,"E0")])]})],"blendedInto":[makeQuery(id+"F2.opFillet","BLEND_FACE",FACE,{"disambiguationData":[OSD([sQuery(id+"F0.wireOp",EDGE,"E0")])]})]});
            var Q11;
            Q11=makeQuery(id+"F11.opFillet","BLEND_EDGE",EDGE,{"blendedFrom":[makeQuery(id+"F5.opExtrude","CAP_EDGE",EDGE,{"disambiguationData":[OSD([sQuery(id+"F4.wireOp",EDGE,"E18")])],"isStart":true}),makeQuery(id+"F2.opFillet","BLEND_FACE",FACE,{"disambiguationData":[OSD([sQuery(id+"F0.wireOp",EDGE,"E0")])]})],"blendedInto":[makeQuery(id+"F2.opFillet","BLEND_FACE",FACE,{"disambiguationData":[OSD([sQuery(id+"F0.wireOp",EDGE,"E0")])]})]});
            var Q12;
            Q12=makeQuery(id+"F23.opFillet","BLEND_EDGE",EDGE,{"blendedFrom":[makeQuery(id+"F9.opExtrude","CAP_EDGE",EDGE,{"disambiguationData":[OSD([sQuery(id+"F8.wireOp",EDGE,"E94.trimOffspring")])],"isStart":true}),makeQuery(id+"F2.opFillet","BLEND_FACE",FACE,{"disambiguationData":[OSD([sQuery(id+"F0.wireOp",EDGE,"E0")])]})],"blendedInto":[makeQuery(id+"F2.opFillet","BLEND_FACE",FACE,{"disambiguationData":[OSD([sQuery(id+"F0.wireOp",EDGE,"E0")])]})]});
            var Q13;
            Q13=makeQuery(id+"F21.opFillet","BLEND_EDGE",EDGE,{"blendedFrom":[makeQuery(id+"F9.opExtrude","CAP_EDGE",EDGE,{"disambiguationData":[OSD([sQuery(id+"F8.wireOp",EDGE,"E81")])],"isStart":true}),makeQuery(id+"F2.opFillet","BLEND_FACE",FACE,{"disambiguationData":[OSD([sQuery(id+"F0.wireOp",EDGE,"E0")])]})],"blendedInto":[makeQuery(id+"F2.opFillet","BLEND_FACE",FACE,{"disambiguationData":[OSD([sQuery(id+"F0.wireOp",EDGE,"E0")])]})]});
            var Q14;
            Q14=makeQuery(id+"F14.opFillet","BLEND_EDGE",EDGE,{"blendedFrom":[makeQuery(id+"F5.opExtrude","CAP_EDGE",EDGE,{"disambiguationData":[OSD([sQuery(id+"F4.wireOp",EDGE,"E32.trimOffspring")])],"isStart":true}),makeQuery(id+"F2.opFillet","BLEND_FACE",FACE,{"disambiguationData":[OSD([sQuery(id+"F0.wireOp",EDGE,"E0")])]})],"blendedInto":[makeQuery(id+"F2.opFillet","BLEND_FACE",FACE,{"disambiguationData":[OSD([sQuery(id+"F0.wireOp",EDGE,"E0")])]})]});
            var Q15;
            Q15=makeQuery(id+"F18.opFillet","BLEND_EDGE",EDGE,{"blendedFrom":[makeQuery(id+"F9.opExtrude","CAP_EDGE",EDGE,{"disambiguationData":[OSD([sQuery(id+"F8.wireOp",EDGE,"E82")])],"isStart":true}),makeQuery(id+"F2.opFillet","BLEND_FACE",FACE,{"disambiguationData":[OSD([sQuery(id+"F0.wireOp",EDGE,"E0")])]})],"blendedInto":[makeQuery(id+"F2.opFillet","BLEND_FACE",FACE,{"disambiguationData":[OSD([sQuery(id+"F0.wireOp",EDGE,"E0")])]})]});
            var Q16;
            Q16=makeQuery(id+"F17.opFillet","BLEND_EDGE",EDGE,{"blendedFrom":[makeQuery(id+"F5.opExtrude","CAP_EDGE",EDGE,{"disambiguationData":[OSD([sQuery(id+"F4.wireOp",EDGE,"E17")])],"isStart":true}),makeQuery(id+"F2.opFillet","BLEND_FACE",FACE,{"disambiguationData":[OSD([sQuery(id+"F0.wireOp",EDGE,"E0")])]})],"blendedInto":[makeQuery(id+"F2.opFillet","BLEND_FACE",FACE,{"disambiguationData":[OSD([sQuery(id+"F0.wireOp",EDGE,"E0")])]})]});
            var Q17;
            Q17=makeQuery(id+"F15.opFillet","BLEND_EDGE",EDGE,{"blendedFrom":[makeQuery(id+"F5.opExtrude","CAP_EDGE",EDGE,{"disambiguationData":[OSD([sQuery(id+"F4.wireOp",EDGE,"E30.trimOffspring")])],"isStart":true}),makeQuery(id+"F2.opFillet","BLEND_FACE",FACE,{"disambiguationData":[OSD([sQuery(id+"F0.wireOp",EDGE,"E0")])]})],"blendedInto":[makeQuery(id+"F2.opFillet","BLEND_FACE",FACE,{"disambiguationData":[OSD([sQuery(id+"F0.wireOp",EDGE,"E0")])]})]});
            fillet(context, id + "F28", {"entities" : qUnion([Q0, Q1, Q2, Q3, Q4, Q5, Q6, Q7, Q8, Q9, Q10, Q11, Q12, Q13, Q14, Q15, Q16, Q17]), "radius" : 2.25 * mm, "tangentPropagation" : true, "allowEdgeOverflow" : false});
        }
    });
